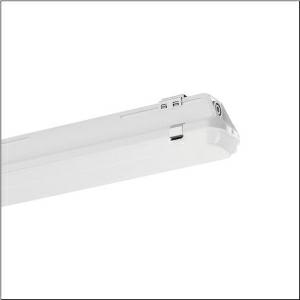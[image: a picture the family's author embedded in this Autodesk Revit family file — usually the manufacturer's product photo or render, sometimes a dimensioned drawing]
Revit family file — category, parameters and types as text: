
# Revit family: monsun_r__21_51fb107p480b005_c053
name_source: partatom
category: Lighting Fixtures
units: mm (PartAtom-declared; Revit-internal decimal feet)

## family parameters
Cut with Voids When Loaded = No
Host = Face
Light Source = No
Part Type = Normal
Room Calculation Point = No
Round Connector Dimension = Use Diameter
Shared = No

## types (1)
- Monsun® 21 (1 x LED, 8070 lm, 52.8 W, 4000K)
    Apparent Load = 53 VA
    CIE Flux Codes = 47 77 93 94 100
    Color Rendering = 80
    Color Temperature = 4000K
    Default Elevation = 1800 mm
    Description = Monsun® 21, damp-proof luminaire, chain hanger, primary optical cover: enclosure, of PMMA, light emission: direct distribution, primary light characteristic: symmetric, installation type: suspended mounting, surface-mounted, horizontal mounting, vertical mounting, LED, rated luminous flux: 8.070lm, luminous efficacy: 153lm/W, light colour: 840, colour temperature: 4000K, control gear: ECG, with terminal, 3-pole, max. 2.5mm², through-wiring: 5x 2.5mm², mains connection: 220..240V, AC, 50/60Hz, rated input power: 53W, housing, of glass-fibre reinforced polyester, uncoated, bright grey, length: 1.590mm, width: 90mm, height: 88mm, clip for enclosure, of stainless steel (V2A), ceiling mounting element, of stainless steel (V2A), chain hanger, of stainless steel (V2A), protection rating (complete): IP66, insulation class (complete): insulation class I (protective earthing), certification: CE, ENEC, VDE, UKCA, protection symbol: D, impact resistance: IK04, permissible operating ambient temperature: -25..+35°C, standard: EN 50419, EN 60598-2-1, corresponds to IFS (International Featured Standards) requirements for safety and quality in the food industry, for indoor or canopied outdoor use, no direct snow, no direct sun, no direct rain, packaging unit: 1 piece
    Height = 89 mm
    Lamp = 1 x LED
    Lamp Light Flux = 8070 lm
    Lamp Power = 52.8 W
    Lamp count = 1
    Length = 1590 mm
    Luminous efficacy = 153 lm/W
    Manufacturer = Siteco
    ModVariant = No
    Model = 51FB107P480B005
    Mounting Place = Ceiling
    Mounting Type = Pendant
    Number of Poles = 1
    OnlyDefault = Yes
    Power Factor = 1
    Product Name = Monsun® 21
    Product group = damp-proof luminaire | ceiling pendant
    ProductGroupID = 908
    Protection Class = Protection class I
    Protection Degree = IP 66
    RLX_Detail_Level = 1
    RlxData = <blob elided: 88121 chars, md5=662b91de>
    Socket = socket
    Standby Power = 0 W
    System Light Flux = 8070 lm
    System Power = 53 W
    Type Comments = Product without accessories
    Type Image = l_1006717.jpg
    URL = http://relux.com
    VarID = ---
    Voltage = 0 V
    Weight = 0.00 kg
    Width = 90 mm

## geometry (parser evidence)
native form markers: Blend x4, Sweep x12
no freeform markers — native parametric forms only
